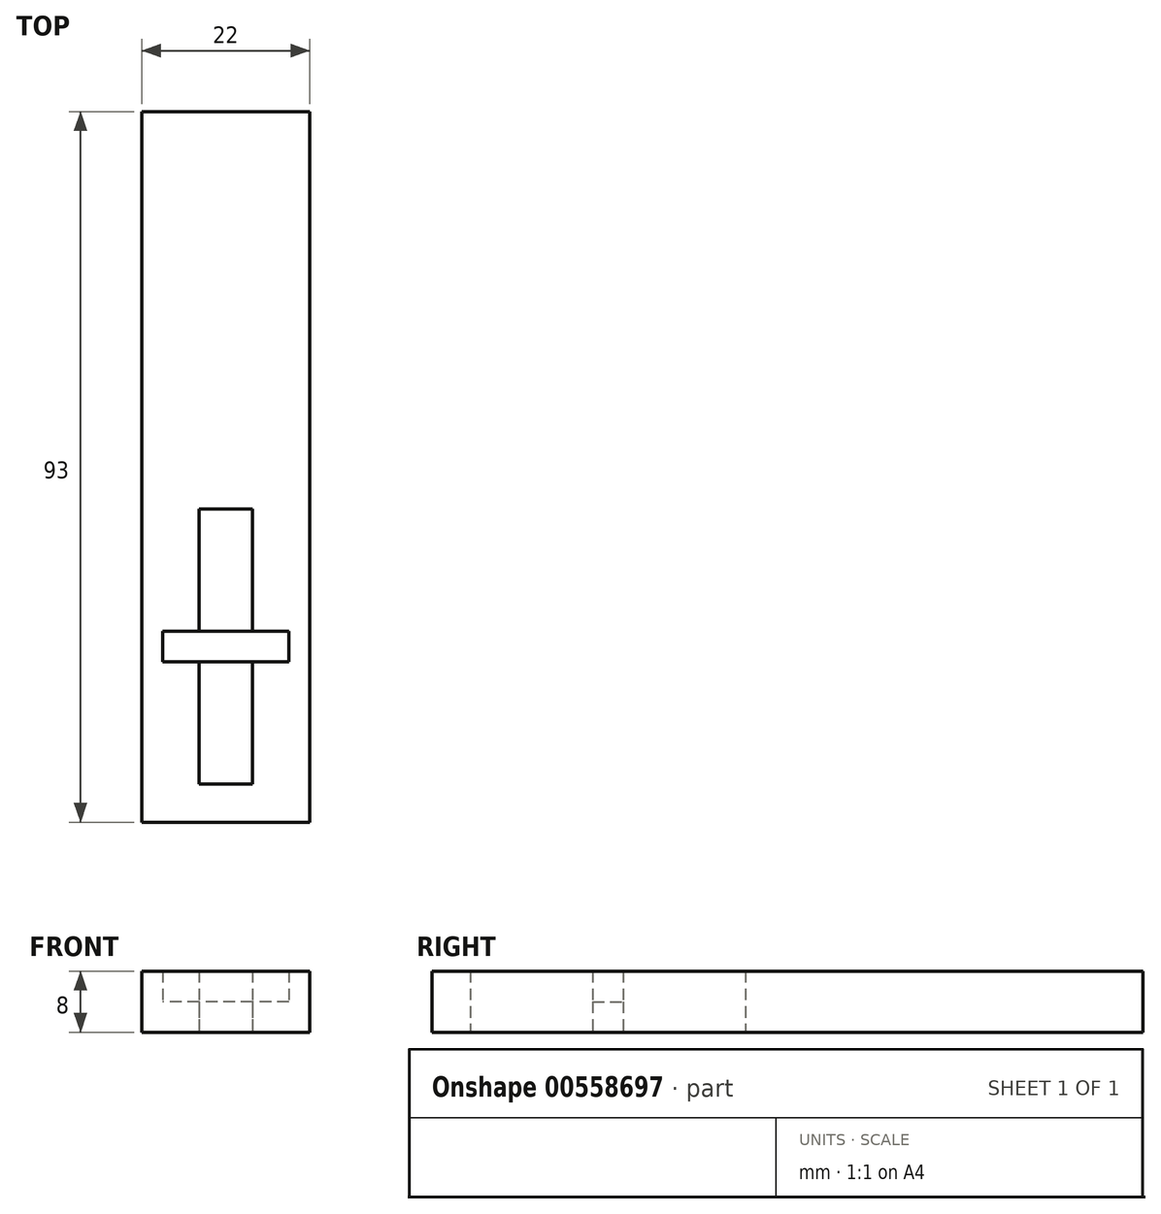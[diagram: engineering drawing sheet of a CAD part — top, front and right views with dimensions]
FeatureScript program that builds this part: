
annotation { "Feature Type Name" : "Feature", "Feature Type Description" : "" }
export const myFeature = defineFeature(function(context is Context, id is Id, definition is map)
    precondition{}
    {
        {
            var Q0;
            Q0=qCreatedBy(makeId("Top.planeOp"),FACE);
            var sketch = newSketch(context, id + "F0", { "sketchPlane" : qUnion([Q0])});
            skLineSegment(sketch, "E0.bottom", {"start": v(11, 46.5) * mm, "end": v(-11, 46.5) * mm});
            skLineSegment(sketch, "E0.top", {"start": v(11, -46.5) * mm, "end": v(-11, -46.5) * mm});
            skLineSegment(sketch, "E0.left", {"start": v(11, 46.5) * mm, "end": v(11, -46.5) * mm});
            skLineSegment(sketch, "E0.right", {"start": v(-11, 46.5) * mm, "end": v(-11, -46.5) * mm});
            skPoint(sketch, "E0.middle", {"position": v(0, 0) * mm});
            skLineSegment(sketch, "E1.bottom", {"start": v(8.25, -25.5) * mm, "end": v(-8.25, -25.5) * mm});
            skLineSegment(sketch, "E1.top", {"start": v(8.25, -21.5) * mm, "end": v(-8.25, -21.5) * mm});
            skLineSegment(sketch, "E1.left", {"start": v(8.25, -25.5) * mm, "end": v(8.25, -21.5) * mm});
            skLineSegment(sketch, "E1.right", {"start": v(-8.25, -25.5) * mm, "end": v(-8.25, -21.5) * mm});
            skPoint(sketch, "E1.middle", {"position": v(0, -23.5) * mm});
            skLineSegment(sketch, "E2.bottom", {"start": v(3.5, -21.5) * mm, "end": v(-3.5, -21.5) * mm});
            skLineSegment(sketch, "E2.top", {"start": v(3.5, -5.5) * mm, "end": v(-3.5, -5.5) * mm});
            skLineSegment(sketch, "E2.left", {"start": v(3.5, -21.5) * mm, "end": v(3.5, -5.5) * mm});
            skLineSegment(sketch, "E2.right", {"start": v(-3.5, -21.5) * mm, "end": v(-3.5, -5.5) * mm});
            skPoint(sketch, "E2.middle", {"position": v(0, -13.5) * mm});
            skLineSegment(sketch, "E3.bottom", {"start": v(3.5, -25.5) * mm, "end": v(-3.5, -25.5) * mm});
            skLineSegment(sketch, "E3.top", {"start": v(3.5, -41.5) * mm, "end": v(-3.5, -41.5) * mm});
            skLineSegment(sketch, "E3.left", {"start": v(3.5, -25.5) * mm, "end": v(3.5, -41.5) * mm});
            skLineSegment(sketch, "E3.right", {"start": v(-3.5, -25.5) * mm, "end": v(-3.5, -41.5) * mm});
            skPoint(sketch, "E3.middle", {"position": v(0, -33.5) * mm});
            skLineSegment(sketch, "E4.bottom", {"start": v(11, 46.5) * mm, "end": v(0, 46.5) * mm});
            skLineSegment(sketch, "E4.top", {"start": v(11, 66.5) * mm, "end": v(0, 66.5) * mm});
            skLineSegment(sketch, "E4.left", {"start": v(11, 46.5) * mm, "end": v(11, 66.5) * mm});
            skLineSegment(sketch, "E4.right", {"start": v(0, 46.5) * mm, "end": v(0, 66.5) * mm});
            skLineSegment(sketch, "E5.bottom", {"start": v(-11, 46.5) * mm, "end": v(0, 46.5) * mm});
            skLineSegment(sketch, "E5.top", {"start": v(-11, 66.5) * mm, "end": v(0, 66.5) * mm});
            skLineSegment(sketch, "E5.left", {"start": v(-11, 46.5) * mm, "end": v(-11, 66.5) * mm});
            skSolve(sketch);
        }
        {
            var Q0;
            Q0=makeQuery(id+"F0.imprint","IMPRINT",FACE,{"disambiguationData":[TD([[makeQuery(id+"F0.imprint","IMPRINT",EDGE,{"derivedFrom":sQuery(id+"F0.wireOp",EDGE,"E0.bottom")}),1.0]])]});
            var Q1;
            Q1=makeQuery(id+"F0.imprint","IMPRINT",FACE,{"disambiguationData":[TD([[makeQuery(id+"F0.imprint","IMPRINT",EDGE,{"derivedFrom":sQuery(id+"F0.wireOp",EDGE,"E0.top")}),-1.0]])]});
            extrude(context, id + "F1", {"entities" : qUnion([Q0, Q1]), "depth" : 8 * mm, "offsetDistance" : 25 * mm});
        }
        {
            var Q0;
            Q0=makeQuery(id+"F0.imprint","IMPRINT",FACE,{"disambiguationData":[TD([[makeQuery(id+"F0.imprint","IMPRINT",EDGE,{"derivedFrom":sQuery(id+"F0.wireOp",EDGE,"E4.bottom")}),-1.0]])]});
            var Q1;
            Q1=makeQuery(id+"F0.imprint","IMPRINT",FACE,{"disambiguationData":[TD([[makeQuery(id+"F0.imprint","IMPRINT",EDGE,{"derivedFrom":sQuery(id+"F0.wireOp",EDGE,"E2.bottom")}),-1.0]])]});
            var Q2;
            {var subQ3=sQuery(id+"F0.wireOp",EDGE,"E1.left");Q2=makeQuery(id+"F0.imprint","IMPRINT",FACE,{"disambiguationData":[TD([[makeQuery(id+"F0.imprint","IMPRINT",EDGE,{"derivedFrom":subQ3}),1.0]])]});}
            var Q3;
            Q3=makeQuery(id+"F0.imprint","IMPRINT",FACE,{"disambiguationData":[TD([[makeQuery(id+"F0.imprint","IMPRINT",EDGE,{"derivedFrom":sQuery(id+"F0.wireOp",EDGE,"E3.bottom")}),1.0]])]});
            var Q4;
            Q4=makeQuery(id+"F0.imprint","IMPRINT",FACE,{"disambiguationData":[TD([[makeQuery(id+"F0.imprint","IMPRINT",EDGE,{"derivedFrom":sQuery(id+"F0.wireOp",EDGE,"E5.bottom")}),1.0]])]});
            extrude(context, id + "F2", {"entities" : qUnion([Q0, Q1, Q2, Q3, Q4]), "operationType" : NewBodyOperationType.ADD, "depth" : 4 * mm, "offsetDistance" : 25 * mm});
        }
    });
